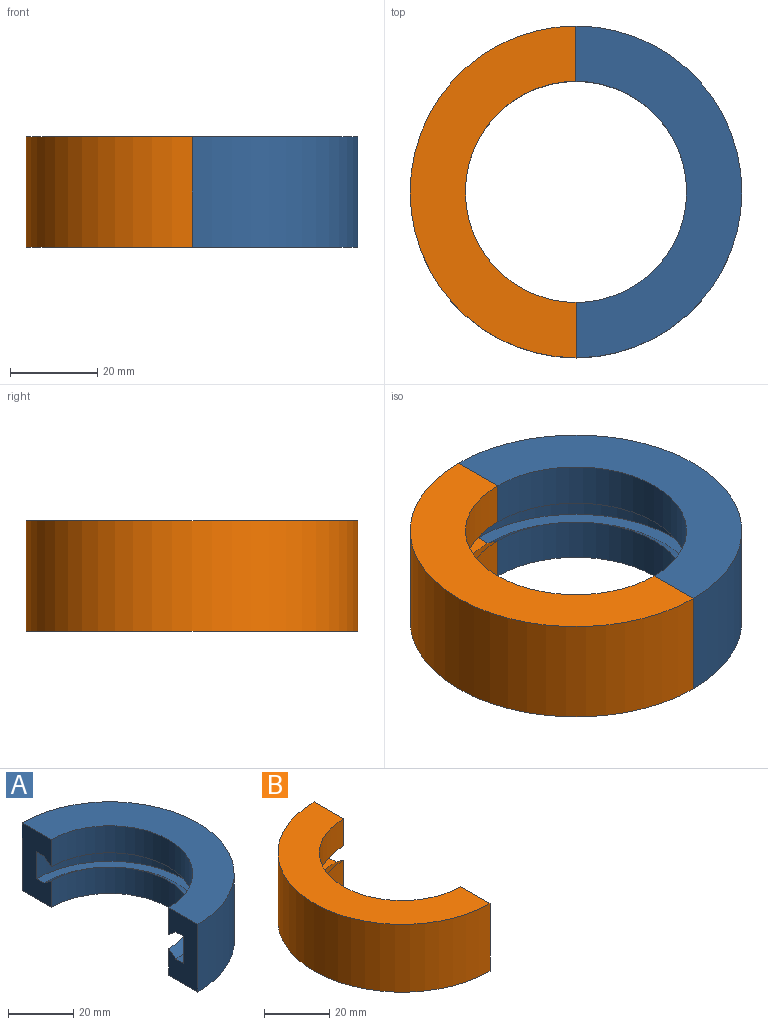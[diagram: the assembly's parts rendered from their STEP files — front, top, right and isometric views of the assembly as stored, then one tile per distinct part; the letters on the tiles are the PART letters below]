
ASSEMBLY  parts=2 mates=1
PART A: 12 faces, bbox 38.1x76.2x25.4 mm
  f0: plane 76.2x38.1mm, normal (0,0,1), area 1266.8mm2, adj f1,f9,f10,f11
  f1: cylinder r=25.4mm len=50.8mm, axis (0,0,1), area 810.7mm2, adj f0,f2,f10,f11
  f2: cone r=28.57mm half-angle=51.3deg, axis (0,0,1), area 344.7mm2, adj f1,f3,f10,f11
  f3: plane 63.5x31.75mm, normal (0,0,-1), area 300.9mm2, adj f2,f4,f10,f11
  f4: cylinder r=31.75mm len=63.5mm, axis (0,0,1), area 1013.4mm2, adj f3,f5,f10,f11
  f5: plane 63.5x31.75mm, normal (0,0,1), area 300.9mm2, adj f4,f6,f10,f11
  f6: cone r=25.4mm half-angle=54.2deg, axis (0,0,-1), area 331.7mm2, adj f5,f7,f10,f11
  f7: cylinder r=25.4mm len=50.8mm, axis (0,0,1), area 790.5mm2, adj f6,f8,f10,f11
  f8: plane 76.2x38.1mm, normal (0,0,-1), area 1266.8mm2, adj f7,f9,f10,f11
  f9: cylinder r=38.1mm len=76.2mm, axis (0,0,1), area 3040.2mm2, adj f0,f8,f10,f11
  f10: plane 25.4x12.7mm, normal (-1,0,0), area 265.7mm2, adj f0,f1,f2,f3,f4,f5,f6,f7
  f11: plane 25.4x12.7mm, normal (-1,0,0), area 265.7mm2, adj f0,f1,f2,f3,f4,f5,f6,f7
PART B: 12 faces, bbox 38.1x76.2x25.4 mm
  f0: plane 76.2x38.1mm, normal (0,0,1), area 1266.8mm2, adj f1,f9,f10,f11
  f1: cylinder r=25.4mm len=50.8mm, axis (0,0,1), area 810.7mm2, adj f0,f2,f10,f11
  f2: cone r=28.57mm half-angle=51.3deg, axis (0,0,1), area 344.7mm2, adj f1,f3,f10,f11
  f3: plane 63.5x31.75mm, normal (0,0,-1), area 300.9mm2, adj f2,f4,f10,f11
  f4: cylinder r=31.75mm len=63.5mm, axis (0,0,1), area 1013.4mm2, adj f3,f5,f10,f11
  f5: plane 63.5x31.75mm, normal (0,0,1), area 300.9mm2, adj f4,f6,f10,f11
  f6: cone r=25.4mm half-angle=54.2deg, axis (0,0,-1), area 331.7mm2, adj f5,f7,f10,f11
  f7: cylinder r=25.4mm len=50.8mm, axis (0,0,1), area 790.5mm2, adj f6,f8,f10,f11
  f8: plane 76.2x38.1mm, normal (0,0,-1), area 1266.8mm2, adj f7,f9,f10,f11
  f9: cylinder r=38.1mm len=76.2mm, axis (0,0,1), area 3040.2mm2, adj f0,f8,f10,f11
  f10: plane 25.4x12.7mm, normal (1,0,0), area 265.7mm2, adj f0,f1,f2,f3,f4,f5,f6,f7
  f11: plane 25.4x12.7mm, normal (1,0,0), area 265.7mm2, adj f0,f1,f2,f3,f4,f5,f6,f7
PLACE A t=(1.67,0.89,-0.11)mm
PLACE B t=(1.67,0.89,-0.11)mm
MATE fastened B.f10 <-> A.f10  axis (1,0,0) through (1.67,-37.21,-0.11)mm
